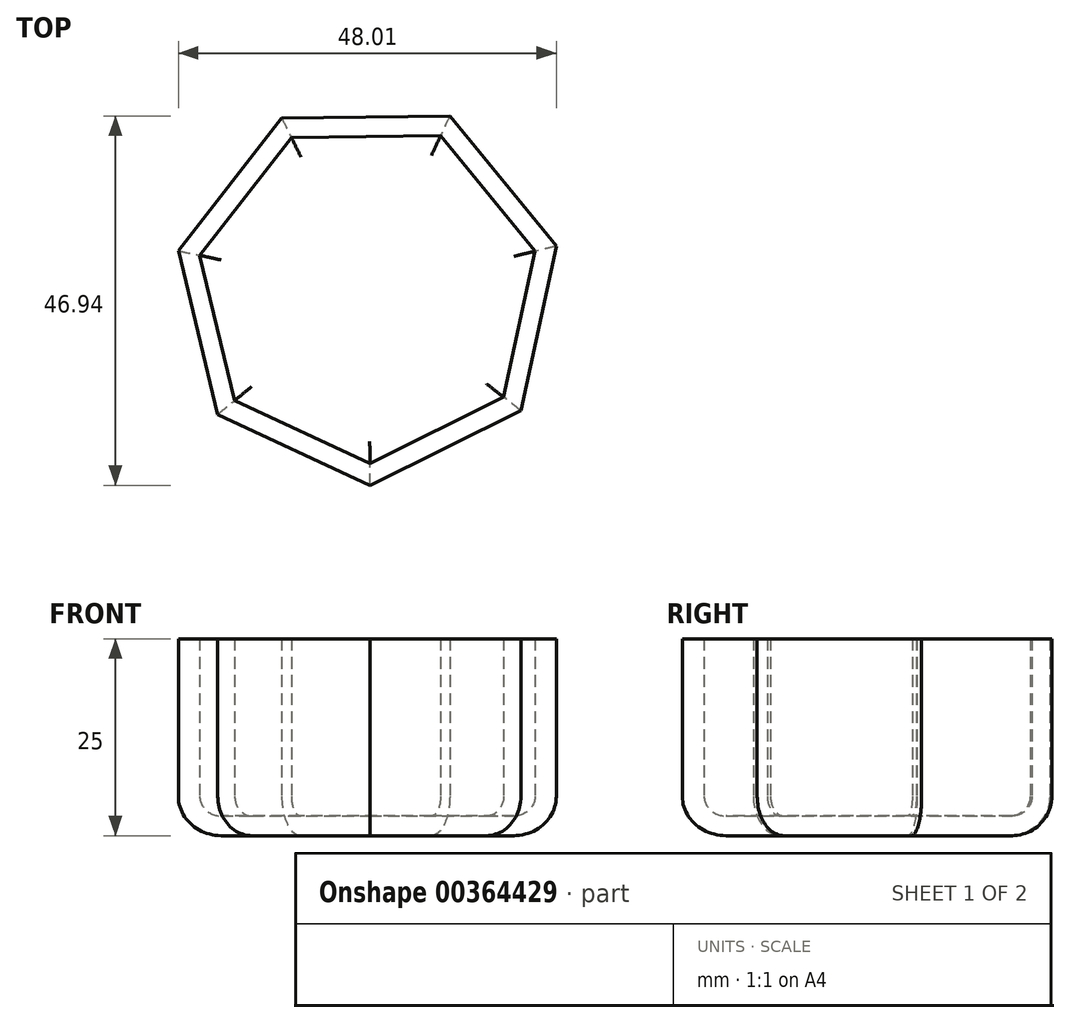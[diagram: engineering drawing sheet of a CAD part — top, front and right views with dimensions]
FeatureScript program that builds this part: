
annotation { "Feature Type Name" : "Feature", "Feature Type Description" : "" }
export const myFeature = defineFeature(function(context is Context, id is Id, definition is map)
    precondition{}
    {
        {
            var Q0;
            Q0=qCreatedBy(makeId("Top.planeOp"),FACE);
            var sketch = newSketch(context, id + "F0", { "sketchPlane" : qUnion([Q0])});
            skCircle(sketch, "E0.cCircle", {"center": v(0, 0) * mm, "radius": 22.19 * mm, "construction": true});
            skLineSegment(sketch, "E0.0", {"start": v(23.94, 5.78) * mm, "end": v(19.44, -15.11) * mm});
            skLineSegment(sketch, "E0.1", {"start": v(19.44, -15.11) * mm, "end": v(0.3, -24.62) * mm});
            skLineSegment(sketch, "E0.2", {"start": v(0.3, -24.62) * mm, "end": v(-19.06, -15.6) * mm});
            skLineSegment(sketch, "E0.3", {"start": v(-19.06, -15.6) * mm, "end": v(-24.07, 5.18) * mm});
            skLineSegment(sketch, "E0.4", {"start": v(-24.07, 5.18) * mm, "end": v(-10.96, 22.05) * mm});
            skLineSegment(sketch, "E0.5", {"start": v(-10.96, 22.05) * mm, "end": v(10.4, 22.32) * mm});
            skLineSegment(sketch, "E0.6", {"start": v(10.4, 22.32) * mm, "end": v(23.94, 5.78) * mm});
            skPoint(sketch, "E0.0.midPoint", {"position": v(21.69, -4.67) * mm});
            skSolve(sketch);
        }
        {
            var Q0;
            Q0 = qSketchRegion(id + "F0", true);
            extrude(context, id + "F1", {"entities" : qUnion([Q0]), "depth" : 25 * mm});
        }
        {
            var Q0;
            Q0=makeQuery(id+"F1.opExtrude","CAP_FACE",FACE,{"disambiguationData":[OSD([sQuery(id+"F0.wireOp",EDGE,"E0.0"),sQuery(id+"F0.wireOp",EDGE,"E0.1"),sQuery(id+"F0.wireOp",EDGE,"E0.2"),sQuery(id+"F0.wireOp",EDGE,"E0.3"),sQuery(id+"F0.wireOp",EDGE,"E0.4"),sQuery(id+"F0.wireOp",EDGE,"E0.5"),sQuery(id+"F0.wireOp",EDGE,"E0.6")])],"isStart":true});
            fillet(context, id + "F2", {"entities" : qUnion([Q0]), "radius" : 5 * mm, "tangentPropagation" : true, "allowEdgeOverflow" : false});
        }
        {
            var Q0;
            Q0=makeQuery(id+"F1.opExtrude","CAP_FACE",FACE,{"disambiguationData":[OSD([sQuery(id+"F0.wireOp",EDGE,"E0.0"),sQuery(id+"F0.wireOp",EDGE,"E0.1"),sQuery(id+"F0.wireOp",EDGE,"E0.2"),sQuery(id+"F0.wireOp",EDGE,"E0.3"),sQuery(id+"F0.wireOp",EDGE,"E0.4"),sQuery(id+"F0.wireOp",EDGE,"E0.5"),sQuery(id+"F0.wireOp",EDGE,"E0.6")])],"isStart":false});
            shell(context, id + "F3", {"entities" : qUnion([Q0]), "thickness" : 2.5 * mm});
        }
    });
